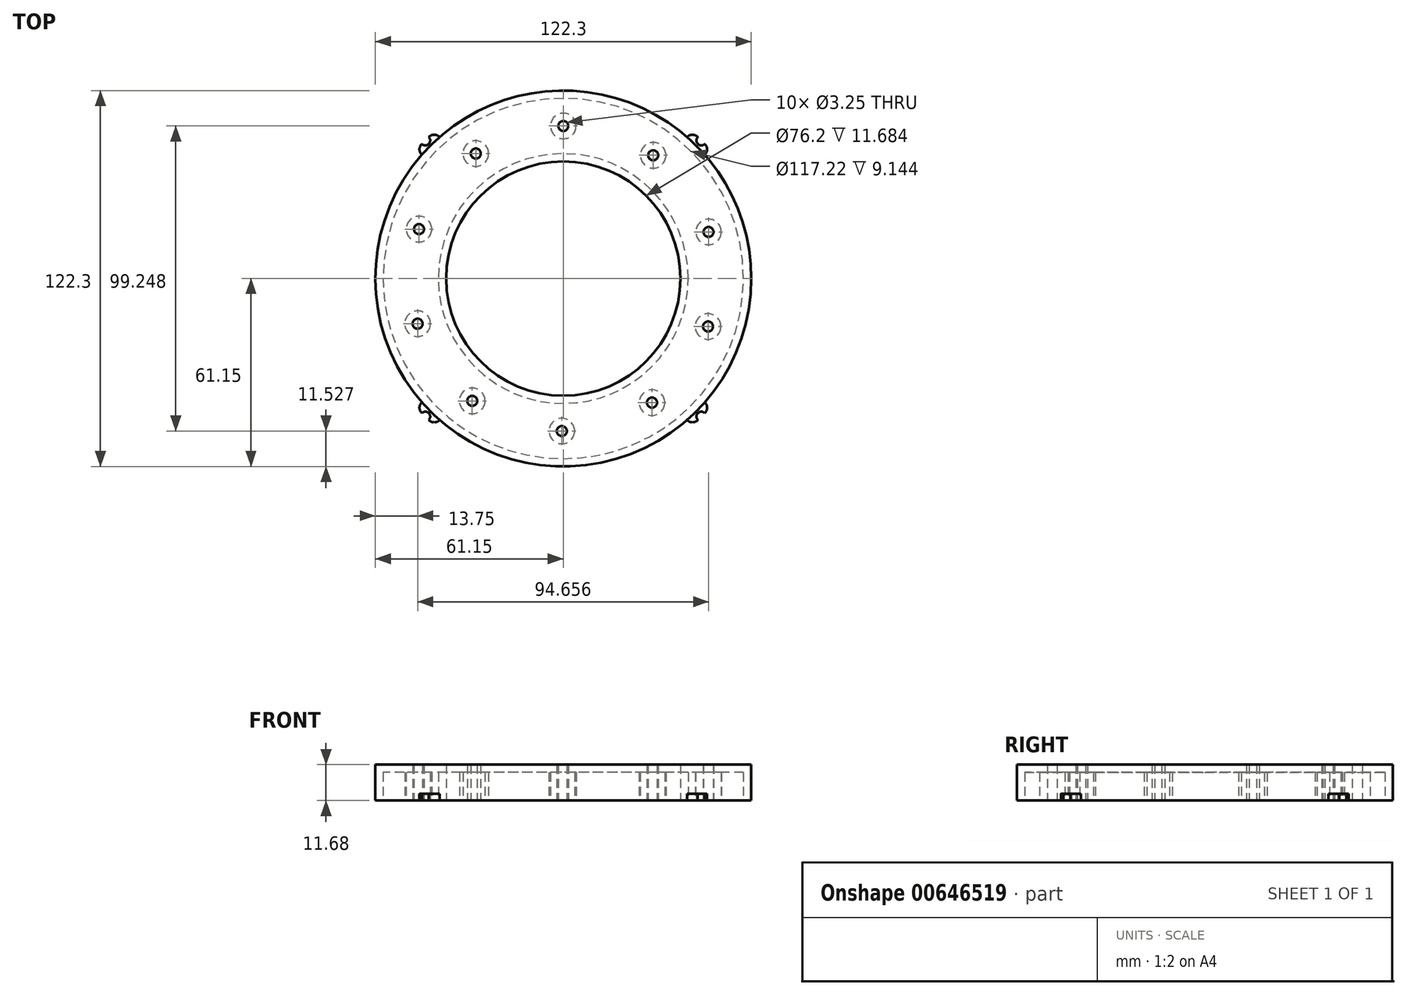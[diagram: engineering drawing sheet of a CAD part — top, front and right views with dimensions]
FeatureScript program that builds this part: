
annotation { "Feature Type Name" : "Feature", "Feature Type Description" : "" }
export const myFeature = defineFeature(function(context is Context, id is Id, definition is map)
    precondition{}
    {
        {
            var Q0;
            Q0=qCreatedBy(makeId("Top.planeOp"),FACE);
            var sketch = newSketch(context, id + "F0", { "sketchPlane" : qUnion([Q0])});
            skArc(sketch, "E0", {"start": v(40.27, 46.02) * mm, "mid": v(0, 61.15) * mm, "end": v(-40.27, 46.02) * mm});
            skCircle(sketch, "E1", {"center": v(0, 0) * mm, "radius": 38.1 * mm});
            skLineSegment(sketch, "E2", {"start": v(0, 38.1) * mm, "end": v(0, 61.15) * mm, "construction": true});
            skCircle(sketch, "E3", {"center": v(0, 49.63) * mm, "radius": 1.63 * mm});
            skCircle(sketch, "E4.1.0", {"center": v(29.25, 40.1) * mm, "radius": 1.63 * mm});
            skCircle(sketch, "E4.2.0", {"center": v(47.26, 15.15) * mm, "radius": 1.63 * mm});
            skCircle(sketch, "E4.3.0", {"center": v(47.1, -15.6) * mm, "radius": 1.63 * mm});
            skCircle(sketch, "E4.4.0", {"center": v(28.86, -40.37) * mm, "radius": 1.63 * mm});
            skCircle(sketch, "E4.5.0", {"center": v(-0.48, -49.62) * mm, "radius": 1.63 * mm});
            skCircle(sketch, "E4.6.0", {"center": v(-29.63, -39.8) * mm, "radius": 1.63 * mm});
            skCircle(sketch, "E4.7.0", {"center": v(-47.4, -14.7) * mm, "radius": 1.63 * mm});
            skCircle(sketch, "E4.8.0", {"center": v(-46.95, 16.07) * mm, "radius": 1.63 * mm});
            skCircle(sketch, "E4.9.0", {"center": v(-28.46, 40.65) * mm, "radius": 1.63 * mm});
            skLineSegment(sketch, "E4.anchor1", {"start": v(0, 0) * mm, "end": v(0, 49.63) * mm, "construction": true});
            skLineSegment(sketch, "E4.anchor2", {"start": v(0, 0) * mm, "end": v(-28.46, 40.65) * mm, "construction": true});
            skCircle(sketch, "E5", {"center": v(0, 0) * mm, "radius": 49.63 * mm, "construction": true});
            skCircle(sketch, "E6", {"center": v(0, 0) * mm, "radius": 63.5 * mm, "construction": true});
            skLineSegment(sketch, "E7", {"start": v(0, 0) * mm, "end": v(63.5, 0) * mm, "construction": true});
            skLineSegment(sketch, "E8", {"start": v(63.5, 0) * mm, "end": v(63.5, 63.5) * mm, "construction": true});
            skLineSegment(sketch, "E9", {"start": v(0, 0) * mm, "end": v(63.5, 63.5) * mm, "construction": true});
            skArc(sketch, "E10", {"start": v(43.76, 46) * mm, "mid": v(43.78, 43.78) * mm, "end": v(46, 43.76) * mm});
            skCircle(sketch, "E11", {"center": v(44.9, 44.9) * mm, "radius": 4.76 * mm, "construction": true});
            skCircle(sketch, "E12", {"center": v(0, 0) * mm, "radius": 62.55 * mm, "construction": true});
            skArc(sketch, "E13", {"start": v(43.76, 46) * mm, "mid": v(42.02, 46.79) * mm, "end": v(40.27, 46.02) * mm});
            skArc(sketch, "E14.MirrorCS", {"start": v(46, 43.76) * mm, "mid": v(46.79, 42.02) * mm, "end": v(46.02, 40.27) * mm});
            skArc(sketch, "E15.trimOffspring", {"start": v(44.43, 42.01) * mm, "mid": v(43.24, 43.24) * mm, "end": v(42.01, 44.43) * mm, "construction": true});
            skArc(sketch, "E16.1.0", {"start": v(46, -43.76) * mm, "mid": v(43.78, -43.78) * mm, "end": v(43.76, -46) * mm});
            skArc(sketch, "E16.1.1", {"start": v(43.76, -46) * mm, "mid": v(42.02, -46.79) * mm, "end": v(40.27, -46.02) * mm});
            skArc(sketch, "E16.1.2", {"start": v(46, -43.76) * mm, "mid": v(46.79, -42.02) * mm, "end": v(46.02, -40.27) * mm});
            skArc(sketch, "E16.2.0", {"start": v(-43.76, -46) * mm, "mid": v(-43.78, -43.78) * mm, "end": v(-46, -43.76) * mm});
            skArc(sketch, "E16.2.1", {"start": v(-46, -43.76) * mm, "mid": v(-46.79, -42.02) * mm, "end": v(-46.02, -40.27) * mm});
            skArc(sketch, "E16.2.2", {"start": v(-43.76, -46) * mm, "mid": v(-42.02, -46.79) * mm, "end": v(-40.27, -46.02) * mm});
            skArc(sketch, "E16.3.0", {"start": v(-46, 43.76) * mm, "mid": v(-43.78, 43.78) * mm, "end": v(-43.76, 46) * mm});
            skArc(sketch, "E16.3.1", {"start": v(-43.76, 46) * mm, "mid": v(-42.02, 46.79) * mm, "end": v(-40.27, 46.02) * mm});
            skArc(sketch, "E16.3.2", {"start": v(-46, 43.76) * mm, "mid": v(-46.79, 42.02) * mm, "end": v(-46.02, 40.27) * mm});
            skArc(sketch, "E17.trimOffspring", {"start": v(42.01, -44.43) * mm, "mid": v(43.24, -43.24) * mm, "end": v(44.43, -42.01) * mm, "construction": true});
            skArc(sketch, "E18.trimOffspring", {"start": v(46.02, -40.27) * mm, "mid": v(61.15, 0) * mm, "end": v(46.02, 40.27) * mm});
            skArc(sketch, "E19.trimOffspring", {"start": v(-44.43, -42.01) * mm, "mid": v(-43.24, -43.24) * mm, "end": v(-42.01, -44.43) * mm, "construction": true});
            skArc(sketch, "E20.trimOffspring", {"start": v(-40.27, -46.02) * mm, "mid": v(0, -61.15) * mm, "end": v(40.27, -46.02) * mm});
            skArc(sketch, "E21.trimOffspring", {"start": v(-46.02, 40.27) * mm, "mid": v(-61.15, 0) * mm, "end": v(-46.02, -40.27) * mm});
            skArc(sketch, "E22.trimOffspring", {"start": v(-42.01, 44.43) * mm, "mid": v(-43.24, 43.24) * mm, "end": v(-44.43, 42.01) * mm, "construction": true});
            skSolve(sketch);
        }
        {
            var Q0;
            Q0=makeQuery(id+"F0.imprint","IMPRINT",FACE,{"disambiguationData":[TD([[makeQuery(id+"F0.imprint","IMPRINT",EDGE,{"derivedFrom":sQuery(id+"F0.wireOp",EDGE,"E0")}),1.0]])]});
            extrude(context, id + "F1", {"entities" : qUnion([Q0]), "depth" : 11.68 * mm, "offsetDistance" : 25.4 * mm});
        }
        {
            var Q0;
            Q0=makeQuery(id+"F1.opExtrude","CAP_FACE",FACE,{"disambiguationData":[OSD([sQuery(id+"F0.wireOp",EDGE,"E0"),sQuery(id+"F0.wireOp",EDGE,"E1"),sQuery(id+"F0.wireOp",EDGE,"E3"),sQuery(id+"F0.wireOp",EDGE,"E4.1.0"),sQuery(id+"F0.wireOp",EDGE,"E4.2.0"),sQuery(id+"F0.wireOp",EDGE,"E4.3.0"),sQuery(id+"F0.wireOp",EDGE,"E4.4.0"),sQuery(id+"F0.wireOp",EDGE,"E4.5.0"),sQuery(id+"F0.wireOp",EDGE,"E4.6.0"),sQuery(id+"F0.wireOp",EDGE,"E4.7.0"),sQuery(id+"F0.wireOp",EDGE,"E4.8.0"),sQuery(id+"F0.wireOp",EDGE,"E4.9.0")])],"isStart":true});
            shell(context, id + "F2", {"entities" : qUnion([Q0]), "thickness" : 2.54 * mm});
        }
        {
            var Q0;
            Q0=makeQuery(id+"F1.opExtrude","CAP_FACE",FACE,{"disambiguationData":[OSD([sQuery(id+"F0.wireOp",EDGE,"E0"),sQuery(id+"F0.wireOp",EDGE,"E1"),sQuery(id+"F0.wireOp",EDGE,"E3"),sQuery(id+"F0.wireOp",EDGE,"E4.1.0"),sQuery(id+"F0.wireOp",EDGE,"E4.2.0"),sQuery(id+"F0.wireOp",EDGE,"E4.3.0"),sQuery(id+"F0.wireOp",EDGE,"E4.4.0"),sQuery(id+"F0.wireOp",EDGE,"E4.5.0"),sQuery(id+"F0.wireOp",EDGE,"E4.6.0"),sQuery(id+"F0.wireOp",EDGE,"E4.7.0"),sQuery(id+"F0.wireOp",EDGE,"E4.8.0"),sQuery(id+"F0.wireOp",EDGE,"E4.9.0"),sQuery(id+"F0.wireOp",EDGE,"E10"),sQuery(id+"F0.wireOp",EDGE,"E13"),sQuery(id+"F0.wireOp",EDGE,"E14.MirrorCS"),sQuery(id+"F0.wireOp",EDGE,"E16.1.0"),sQuery(id+"F0.wireOp",EDGE,"E16.1.1"),sQuery(id+"F0.wireOp",EDGE,"E16.1.2"),sQuery(id+"F0.wireOp",EDGE,"E16.2.0"),sQuery(id+"F0.wireOp",EDGE,"E16.2.1"),sQuery(id+"F0.wireOp",EDGE,"E16.2.2"),sQuery(id+"F0.wireOp",EDGE,"E16.3.0"),sQuery(id+"F0.wireOp",EDGE,"E16.3.1"),sQuery(id+"F0.wireOp",EDGE,"E16.3.2"),sQuery(id+"F0.wireOp",EDGE,"E18.trimOffspring"),sQuery(id+"F0.wireOp",EDGE,"E20.trimOffspring"),sQuery(id+"F0.wireOp",EDGE,"E21.trimOffspring")])],"isStart":false});
            var sketch = newSketch(context, id + "F3", { "sketchPlane" : qUnion([Q0])});
            skCircle(sketch, "E23", {"center": v(0, 0) * mm, "radius": 61.15 * mm});
            skSolve(sketch);
        }
        {
            var Q0;
            Q0=makeQuery(id+"F3.imprint","IMPRINT",FACE,{"disambiguationData":[TD([[makeQuery(id+"F3.imprint","IMPRINT",EDGE,{"derivedFrom":makeQuery(id+"F1.opExtrude","CAP_EDGE",EDGE,{"disambiguationData":[OSD([sQuery(id+"F0.wireOp",EDGE,"E16.3.0")])],"isStart":false})}),-1.0]])]});
            var Q1;
            Q1=makeQuery(id+"F3.imprint","IMPRINT",FACE,{"disambiguationData":[TD([[makeQuery(id+"F3.imprint","IMPRINT",EDGE,{"derivedFrom":makeQuery(id+"F1.opExtrude","CAP_EDGE",EDGE,{"disambiguationData":[OSD([sQuery(id+"F0.wireOp",EDGE,"E16.2.0")])],"isStart":false})}),-1.0]])]});
            var Q2;
            Q2=makeQuery(id+"F3.imprint","IMPRINT",FACE,{"disambiguationData":[TD([[makeQuery(id+"F3.imprint","IMPRINT",EDGE,{"derivedFrom":makeQuery(id+"F1.opExtrude","CAP_EDGE",EDGE,{"disambiguationData":[OSD([sQuery(id+"F0.wireOp",EDGE,"E16.1.0")])],"isStart":false})}),-1.0]])]});
            var Q3;
            Q3=makeQuery(id+"F3.imprint","IMPRINT",FACE,{"disambiguationData":[TD([[makeQuery(id+"F3.imprint","IMPRINT",EDGE,{"derivedFrom":makeQuery(id+"F1.opExtrude","CAP_EDGE",EDGE,{"disambiguationData":[OSD([sQuery(id+"F0.wireOp",EDGE,"E10")])],"isStart":false})}),-1.0]])]});
            extrude(context, id + "F4", {"entities" : qUnion([Q0, Q1, Q2, Q3]), "operationType" : NewBodyOperationType.REMOVE, "oppositeDirection" : true, "depth" : 9.52 * mm, "offsetDistance" : 25.4 * mm});
        }
    });
